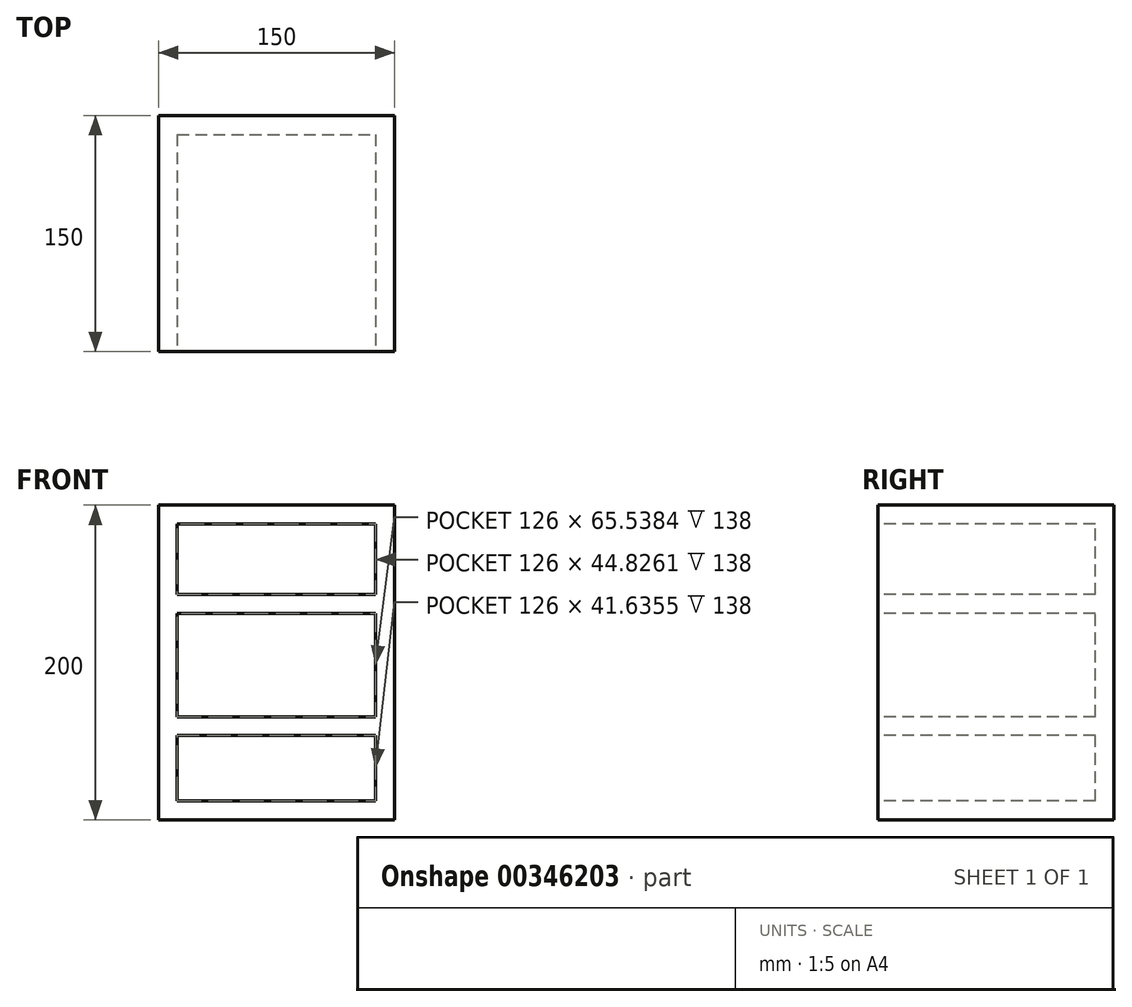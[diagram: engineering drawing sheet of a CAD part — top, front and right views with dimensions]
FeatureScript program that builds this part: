
annotation { "Feature Type Name" : "Feature", "Feature Type Description" : "" }
export const myFeature = defineFeature(function(context is Context, id is Id, definition is map)
    precondition{}
    {
        {
            var Q0;
            Q0=qCreatedBy(makeId("Front.planeOp"),FACE);
            var sketch = newSketch(context, id + "F0", { "sketchPlane" : qUnion([Q0])});
            skLineSegment(sketch, "E0.bottom", {"start": v(-75, -100) * mm, "end": v(75, -100) * mm});
            skLineSegment(sketch, "E0.top", {"start": v(-75, 100) * mm, "end": v(75, 100) * mm});
            skLineSegment(sketch, "E0.left", {"start": v(-75, -100) * mm, "end": v(-75, 100) * mm});
            skLineSegment(sketch, "E0.right", {"start": v(75, -100) * mm, "end": v(75, 100) * mm});
            skPoint(sketch, "E0.middle", {"position": v(0, 0) * mm});
            skSolve(sketch);
        }
        {
            var Q0;
            Q0=makeQuery(id+"F0.imprint","IMPRINT",FACE,{"disambiguationData":[TD([[makeQuery(id+"F0.imprint","IMPRINT",EDGE,{"derivedFrom":sQuery(id+"F0.wireOp",EDGE,"E0.bottom")}),1.0]])]});
            extrude(context, id + "F1", {"entities" : qUnion([Q0]), "oppositeDirection" : true, "depth" : 150 * mm});
        }
        {
            var Q0;
            Q0=makeQuery(id+"F1.opExtrude","CAP_FACE",FACE,{"disambiguationData":[OSD([sQuery(id+"F0.wireOp",EDGE,"E0.bottom"),sQuery(id+"F0.wireOp",EDGE,"E0.top"),sQuery(id+"F0.wireOp",EDGE,"E0.left"),sQuery(id+"F0.wireOp",EDGE,"E0.right")])],"isStart":true});
            shell(context, id + "F2", {"entities" : qUnion([Q0]), "thickness" : 12 * mm});
        }
        {
            var Q0;
            Q0=makeQuery(id+"F1.opExtrude","CAP_FACE",FACE,{"disambiguationData":[OSD([sQuery(id+"F0.wireOp",EDGE,"E0.bottom"),sQuery(id+"F0.wireOp",EDGE,"E0.top"),sQuery(id+"F0.wireOp",EDGE,"E0.left"),sQuery(id+"F0.wireOp",EDGE,"E0.right")])],"isStart":true});
            var sketch = newSketch(context, id + "F3", { "sketchPlane" : qUnion([Q0])});
            skLineSegment(sketch, "E1.bottom", {"start": v(-71.68, 31.17) * mm, "end": v(72.32, 31.17) * mm});
            skLineSegment(sketch, "E1.top", {"start": v(-71.68, 43.17) * mm, "end": v(72.32, 43.17) * mm});
            skLineSegment(sketch, "E1.left", {"start": v(-71.68, 31.17) * mm, "end": v(-71.68, 43.17) * mm});
            skLineSegment(sketch, "E1.right", {"start": v(72.32, 31.17) * mm, "end": v(72.32, 43.17) * mm});
            skLineSegment(sketch, "E2.bottom", {"start": v(-72.6, -34.36) * mm, "end": v(72.32, -34.36) * mm});
            skLineSegment(sketch, "E2.top", {"start": v(-72.6, -46.36) * mm, "end": v(72.32, -46.36) * mm});
            skLineSegment(sketch, "E2.left", {"start": v(-72.6, -34.36) * mm, "end": v(-72.6, -46.36) * mm});
            skLineSegment(sketch, "E2.right", {"start": v(72.32, -34.36) * mm, "end": v(72.32, -46.36) * mm});
            skSolve(sketch);
        }
        {
            var Q0;
            {var subQ0=sQuery(id+"F3.wireOp",EDGE,"E1.bottom");var subQ1=sQuery(id+"F0.wireOp",EDGE,"E0.left");var subQ2=makeQuery(id+"F2.opShell","OFFSET_EDGE",EDGE,{"disambiguationData":[OSD([subQ1]),TDD([makeQuery(id+"F1.opExtrude","CAP_EDGE",EDGE,{"disambiguationData":[OSD([subQ1])],"isStart":true})])]});var subQ3=makeQuery(id+"F3.imprint","INTERSECT",VERTEX,{"derivedFrom":[subQ2,subQ0]});Q0=makeQuery(id+"F3.imprint","IMPRINT",FACE,{"disambiguationData":[TD([[makeQuery(id+"F3.imprint","IMPRINT",EDGE,{"disambiguationData":[TD([[subQ3,-1.0]])],"derivedFrom":subQ0}),1.0]])]});}
            var Q1;
            {var subQ0=sQuery(id+"F3.wireOp",EDGE,"E2.bottom");var subQ1=sQuery(id+"F0.wireOp",EDGE,"E0.left");var subQ2=makeQuery(id+"F2.opShell","OFFSET_EDGE",EDGE,{"disambiguationData":[OSD([subQ1]),TDD([makeQuery(id+"F1.opExtrude","CAP_EDGE",EDGE,{"disambiguationData":[OSD([subQ1])],"isStart":true})])]});var subQ3=makeQuery(id+"F3.imprint","INTERSECT",VERTEX,{"derivedFrom":[subQ2,subQ0]});Q1=makeQuery(id+"F3.imprint","IMPRINT",FACE,{"disambiguationData":[TD([[makeQuery(id+"F3.imprint","IMPRINT",EDGE,{"disambiguationData":[TD([[subQ3,-1.0]])],"derivedFrom":subQ0}),-1.0]])]});}
            extrude(context, id + "F4", {"entities" : qUnion([Q0, Q1]), "operationType" : NewBodyOperationType.ADD, "oppositeDirection" : true, "depth" : 140 * mm});
        }
    });
